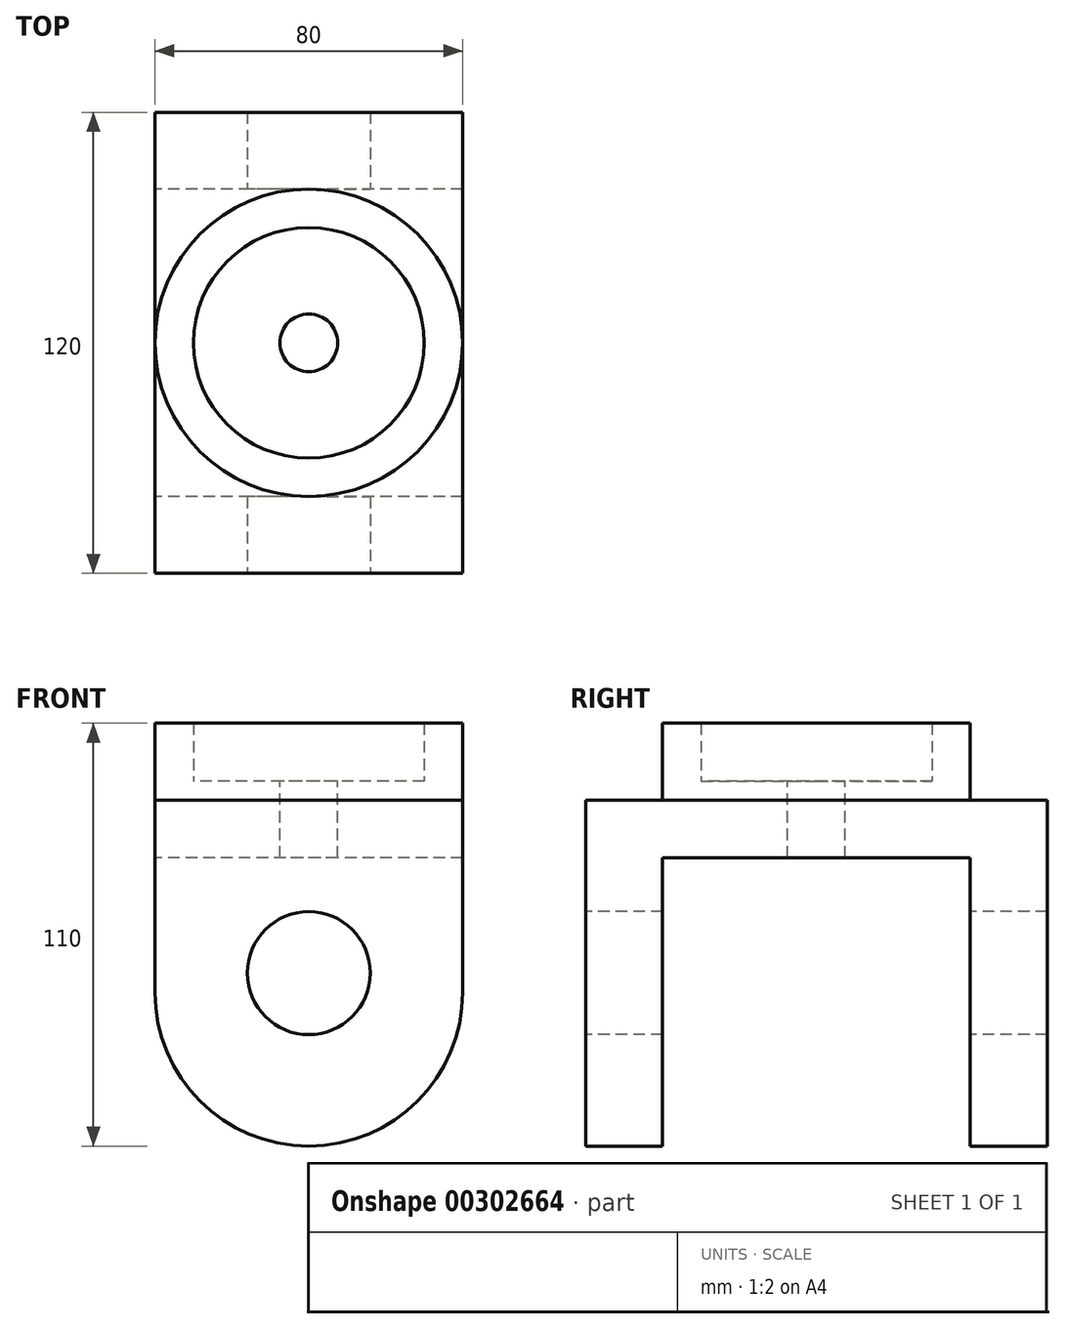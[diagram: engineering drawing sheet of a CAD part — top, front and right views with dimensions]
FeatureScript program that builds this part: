
annotation { "Feature Type Name" : "Feature", "Feature Type Description" : "" }
export const myFeature = defineFeature(function(context is Context, id is Id, definition is map)
    precondition{}
    {
        {
            var Q0;
            Q0=qCreatedBy(makeId("Front.planeOp"),FACE);
            var sketch = newSketch(context, id + "F0", { "sketchPlane" : qUnion([Q0])});
            skLineSegment(sketch, "E0.bottom", {"start": v(40, -45) * mm, "end": v(-40, -45) * mm});
            skLineSegment(sketch, "E0.top", {"start": v(40, 45) * mm, "end": v(-40, 45) * mm});
            skLineSegment(sketch, "E0.left", {"start": v(40, -45) * mm, "end": v(40, 45) * mm});
            skLineSegment(sketch, "E0.right", {"start": v(-40, -45) * mm, "end": v(-40, 45) * mm});
            skPoint(sketch, "E0.middle", {"position": v(0, 0) * mm});
            skSolve(sketch);
        }
        {
            var Q0;
            Q0=makeQuery(id+"F0.imprint","IMPRINT",FACE,{"disambiguationData":[TD([[makeQuery(id+"F0.imprint","IMPRINT",EDGE,{"derivedFrom":sQuery(id+"F0.wireOp",EDGE,"E0.bottom")}),-1.0]])]});
            extrude(context, id + "F1", {"entities" : qUnion([Q0]), "depth" : 60 * mm, "hasSecondDirection" : true, "secondDirectionOppositeDirection" : true, "secondDirectionDepth" : 60 * mm});
        }
        {
            var Q0;
            Q0=makeQuery(id+"F1.opExtrude","SWEPT_EDGE",EDGE,{"disambiguationData":[OSD([sQuery(id+"F0.wireOp",EDGE,"E0.bottom"),sQuery(id+"F0.wireOp",EDGE,"E0.left")])]});
            var Q1;
            Q1=makeQuery(id+"F1.opExtrude","SWEPT_EDGE",EDGE,{"disambiguationData":[OSD([sQuery(id+"F0.wireOp",EDGE,"E0.bottom"),sQuery(id+"F0.wireOp",EDGE,"E0.right")])]});
            fillet(context, id + "F2", {"entities" : qUnion([Q0, Q1]), "radius" : 40 * mm, "tangentPropagation" : true, "allowEdgeOverflow" : false});
        }
        {
            var Q0;
            Q0=makeQuery(id+"F1.opExtrude","CAP_FACE",FACE,{"disambiguationData":[OSD([sQuery(id+"F0.wireOp",EDGE,"E0.bottom"),sQuery(id+"F0.wireOp",EDGE,"E0.top"),sQuery(id+"F0.wireOp",EDGE,"E0.left"),sQuery(id+"F0.wireOp",EDGE,"E0.right")])],"isStart":false});
            var sketch = newSketch(context, id + "F3", { "sketchPlane" : qUnion([Q0])});
            skCircle(sketch, "E1", {"center": v(0, 0) * mm, "radius": 16 * mm});
            skSolve(sketch);
        }
        {
            var Q0;
            Q0=makeQuery(id+"F3.imprint","IMPRINT",FACE,{"disambiguationData":[TD([[makeQuery(id+"F3.imprint","IMPRINT",EDGE,{"derivedFrom":sQuery(id+"F3.wireOp",EDGE,"E1")}),1.0]])]});
            extrude(context, id + "F4", {"entities" : qUnion([Q0]), "operationType" : NewBodyOperationType.REMOVE, "endBound" : BoundingType.THROUGH_ALL, "oppositeDirection" : true, "depth" : 25 * mm});
        }
        {
            var Q0;
            Q0=makeQuery(id+"F1.opExtrude","SWEPT_FACE",FACE,{"disambiguationData":[OSD([sQuery(id+"F0.wireOp",EDGE,"E0.right")])]});
            var sketch = newSketch(context, id + "F5", { "sketchPlane" : qUnion([Q0])});
            skLineSegment(sketch, "E2.bottom", {"start": v(40, 30) * mm, "end": v(-40, 30) * mm});
            skLineSegment(sketch, "E2.top", {"start": v(40, -70) * mm, "end": v(-40, -70) * mm});
            skLineSegment(sketch, "E2.left", {"start": v(40, 30) * mm, "end": v(40, -70) * mm});
            skLineSegment(sketch, "E2.right", {"start": v(-40, 30) * mm, "end": v(-40, -70) * mm});
            skPoint(sketch, "E2.middle", {"position": v(0, -20) * mm});
            skPoint(sketch, "E2.middle.positionSnap0", {"position": v(0, -5) * mm});
            skPoint(sketch, "E2.centerSnap0", {"position": v(0, -5) * mm});
            skSolve(sketch);
        }
        {
            var Q0;
            {var subQ0=sQuery(id+"F5.wireOp",EDGE,"E2.top");Q0=makeQuery(id+"F5.imprint","IMPRINT",FACE,{"disambiguationData":[TD([[makeQuery(id+"F5.imprint","IMPRINT",EDGE,{"derivedFrom":subQ0}),-1.0]])]});}
            var Q1;
            {var subQ0=sQuery(id+"F5.wireOp",EDGE,"E2.bottom");Q1=makeQuery(id+"F5.imprint","IMPRINT",FACE,{"disambiguationData":[TD([[makeQuery(id+"F5.imprint","IMPRINT",EDGE,{"derivedFrom":subQ0}),1.0]])]});}
            extrude(context, id + "F6", {"entities" : qUnion([Q0, Q1]), "operationType" : NewBodyOperationType.REMOVE, "endBound" : BoundingType.THROUGH_ALL, "oppositeDirection" : true, "depth" : 25 * mm});
        }
        {
            var Q0;
            Q0=makeQuery(id+"F1.opExtrude","SWEPT_FACE",FACE,{"disambiguationData":[OSD([sQuery(id+"F0.wireOp",EDGE,"E0.top")])]});
            var sketch = newSketch(context, id + "F7", { "sketchPlane" : qUnion([Q0])});
            skCircle(sketch, "E3", {"center": v(0, 0) * mm, "radius": 7.5 * mm});
            skCircle(sketch, "E4", {"center": v(0, 0) * mm, "radius": 30 * mm});
            skCircle(sketch, "E5", {"center": v(0, 0) * mm, "radius": 40 * mm});
            skSolve(sketch);
        }
        {
            var Q0;
            Q0=makeQuery(id+"F7.imprint","IMPRINT",FACE,{"disambiguationData":[TD([[makeQuery(id+"F7.imprint","IMPRINT",EDGE,{"derivedFrom":sQuery(id+"F7.wireOp",EDGE,"E3")}),1.0]])]});
            extrude(context, id + "F8", {"entities" : qUnion([Q0]), "operationType" : NewBodyOperationType.REMOVE, "endBound" : BoundingType.THROUGH_ALL, "oppositeDirection" : true, "depth" : 25 * mm});
        }
        {
            var Q0;
            Q0=makeQuery(id+"F7.imprint","IMPRINT",FACE,{"disambiguationData":[TD([[makeQuery(id+"F7.imprint","IMPRINT",EDGE,{"derivedFrom":sQuery(id+"F7.wireOp",EDGE,"E3")}),-1.0]])]});
            extrude(context, id + "F9", {"entities" : qUnion([Q0]), "operationType" : NewBodyOperationType.ADD, "depth" : 5 * mm});
        }
        {
            var Q0;
            Q0=makeQuery(id+"F7.imprint","IMPRINT",FACE,{"disambiguationData":[TD([[makeQuery(id+"F7.imprint","IMPRINT",EDGE,{"derivedFrom":sQuery(id+"F7.wireOp",EDGE,"E4")}),-1.0]])]});
            extrude(context, id + "F10", {"entities" : qUnion([Q0]), "operationType" : NewBodyOperationType.ADD, "depth" : 20 * mm});
        }
    });
